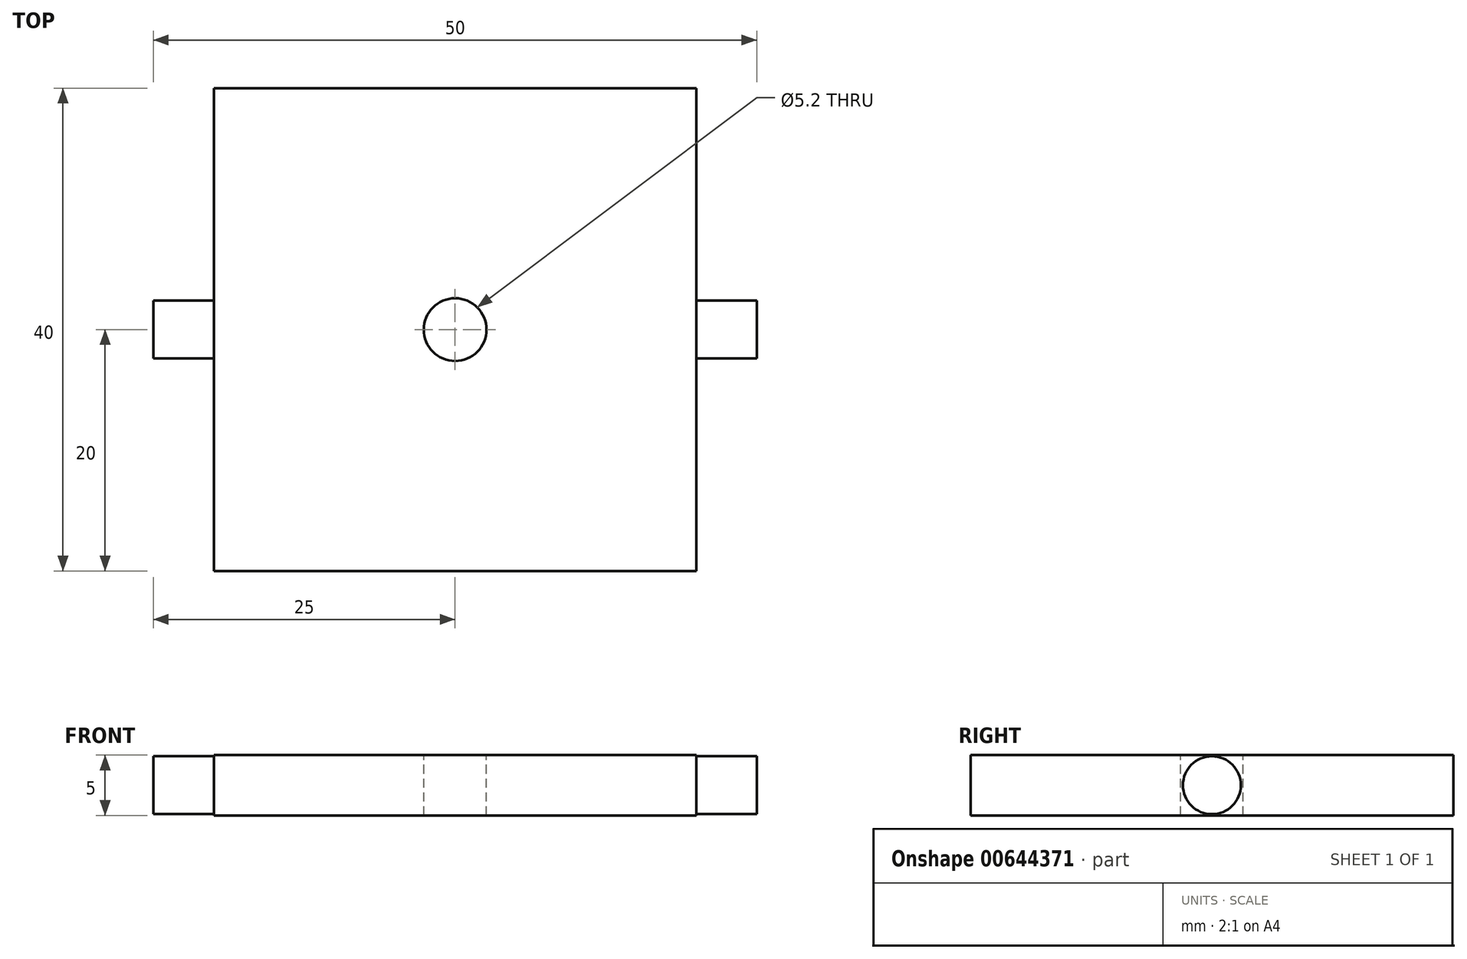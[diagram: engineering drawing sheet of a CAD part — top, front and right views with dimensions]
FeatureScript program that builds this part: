
annotation { "Feature Type Name" : "Feature", "Feature Type Description" : "" }
export const myFeature = defineFeature(function(context is Context, id is Id, definition is map)
    precondition{}
    {
        {
            var Q0;
            Q0=qCreatedBy(makeId("Top.planeOp"),FACE);
            var sketch = newSketch(context, id + "F0", { "sketchPlane" : qUnion([Q0])});
            skLineSegment(sketch, "E0.bottom", {"start": v(20, 20) * mm, "end": v(-20, 20) * mm});
            skLineSegment(sketch, "E0.top", {"start": v(20, -20) * mm, "end": v(-20, -20) * mm});
            skLineSegment(sketch, "E0.left", {"start": v(20, 20) * mm, "end": v(20, -20) * mm});
            skLineSegment(sketch, "E0.right", {"start": v(-20, 20) * mm, "end": v(-20, -20) * mm});
            skPoint(sketch, "E0.middle", {"position": v(0, 0) * mm});
            skSolve(sketch);
        }
        {
            var Q0;
            Q0 = qSketchRegion(id + "F0", true);
            extrude(context, id + "F1", {"entities" : qUnion([Q0]), "depth" : 5 * mm, "offsetDistance" : 25.4 * mm});
        }
        {
            var Q0;
            Q0=makeQuery(id+"F1.opExtrude","CAP_FACE",FACE,{"disambiguationData":[OSD([sQuery(id+"F0.wireOp",EDGE,"E0.bottom"),sQuery(id+"F0.wireOp",EDGE,"E0.top"),sQuery(id+"F0.wireOp",EDGE,"E0.left"),sQuery(id+"F0.wireOp",EDGE,"E0.right")])],"isStart":false});
            var sketch = newSketch(context, id + "F2", { "sketchPlane" : qUnion([Q0])});
            skCircle(sketch, "E1", {"center": v(0, 0) * mm, "radius": 2.6 * mm});
            skSolve(sketch);
        }
        {
            var Q0;
            Q0 = qSketchRegion(id + "F2", true);
            extrude(context, id + "F3", {"entities" : qUnion([Q0]), "operationType" : NewBodyOperationType.REMOVE, "oppositeDirection" : true, "depth" : 25.4 * mm, "offsetDistance" : 25.4 * mm});
        }
        {
            var Q0;
            Q0=makeQuery(id+"F1.opExtrude","SWEPT_FACE",FACE,{"disambiguationData":[OSD([sQuery(id+"F0.wireOp",EDGE,"E0.left")])]});
            var sketch = newSketch(context, id + "F4", { "sketchPlane" : qUnion([Q0])});
            skCircle(sketch, "E2", {"center": v(0, 2.5) * mm, "radius": 2.4 * mm});
            skSolve(sketch);
        }
        {
            var Q0;
            Q0=makeQuery(id+"F4.imprint","IMPRINT",FACE,{"disambiguationData":[TD([[makeQuery(id+"F4.imprint","IMPRINT",EDGE,{"derivedFrom":sQuery(id+"F4.wireOp",EDGE,"E2")}),1.0]])]});
            extrude(context, id + "F5", {"entities" : qUnion([Q0]), "operationType" : NewBodyOperationType.ADD, "depth" : 5 * mm, "offsetDistance" : 25.4 * mm});
        }
        {
            var Q0;
            Q0=makeQuery(id+"F1.opExtrude","SWEPT_BODY",BODY,{"disambiguationData":[OSD([sQuery(id+"F0.wireOp",EDGE,"E0.bottom"),sQuery(id+"F0.wireOp",EDGE,"E0.top"),sQuery(id+"F0.wireOp",EDGE,"E0.left"),sQuery(id+"F0.wireOp",EDGE,"E0.right")])]});
            var Q1;
            Q1=qCreatedBy(makeId("Right.planeOp"),FACE);
            mirror(context, id + "F6", {"operationType" : NewBodyOperationType.ADD, "entities" : qUnion([Q0]), "mirrorPlane" : qUnion([Q1])});
        }
    });
